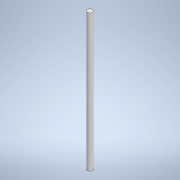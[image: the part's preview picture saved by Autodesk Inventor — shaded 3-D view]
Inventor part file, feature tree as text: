
AUTODESK INVENTOR PART (.ipt)
format: ipt  version: 2022.3 (Build 263350000, 350)  size: 90,624 bytes
history: native  units: mm
features: extrude x1, sketch x1
ambient origin geometry x8: Origin, YZ Plane, XZ Plane, XY Plane, X Axis, Y Axis, Z Axis, Center Point
bodies: Solid1 (feature_tree)
feature tree (2):
  extrude  "Extrusion1"  Depth=210.0mm TaperAngle=0.0deg
  sketch  "Sketch1"  dims[d0=8.0mm d1=210.0mm d2=0.0mm]
